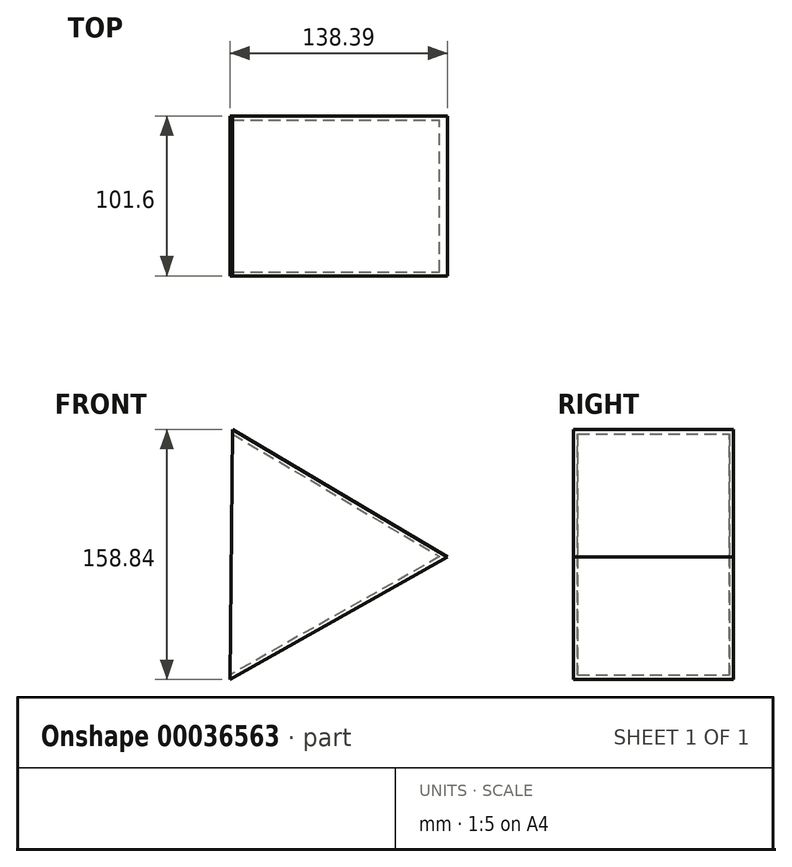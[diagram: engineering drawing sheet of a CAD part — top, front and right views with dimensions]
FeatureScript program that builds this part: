
annotation { "Feature Type Name" : "Feature", "Feature Type Description" : "" }
export const myFeature = defineFeature(function(context is Context, id is Id, definition is map)
    precondition{}
    {
        {
            var Q0;
            Q0=qCreatedBy(makeId("Front.planeOp"),FACE);
            var sketch = newSketch(context, id + "F0", { "sketchPlane" : qUnion([Q0])});
            skCircle(sketch, "E0.cCircle", {"center": v(0, 0) * mm, "radius": 45.85 * mm, "construction": true});
            skLineSegment(sketch, "E0.0", {"start": v(-45.02, 79.9) * mm, "end": v(91.7, -0.96) * mm});
            skLineSegment(sketch, "E0.1", {"start": v(91.7, -0.96) * mm, "end": v(-46.69, -78.94) * mm});
            skLineSegment(sketch, "E0.2", {"start": v(-46.69, -78.94) * mm, "end": v(-45.02, 79.9) * mm});
            skPoint(sketch, "E0.0.midPoint", {"position": v(23.34, 39.47) * mm});
            skSolve(sketch);
        }
        {
            var Q0;
            Q0=makeQuery(id+"F0.imprint","IMPRINT",FACE,{"disambiguationData":[TD([[makeQuery(id+"F0.imprint","IMPRINT",EDGE,{"derivedFrom":sQuery(id+"F0.wireOp",EDGE,"E0.0")}),-1.0]])]});
            extrude(context, id + "F1", {"entities" : qUnion([Q0]), "depth" : 101.6 * mm});
        }
        {
            var Q0;
            Q0=makeQuery(id+"F1.opExtrude","SWEPT_FACE",FACE,{"disambiguationData":[OSD([sQuery(id+"F0.wireOp",EDGE,"E0.2")])]});
            shell(context, id + "F2", {"entities" : qUnion([Q0]), "thickness" : 2.54 * mm});
        }
    });
